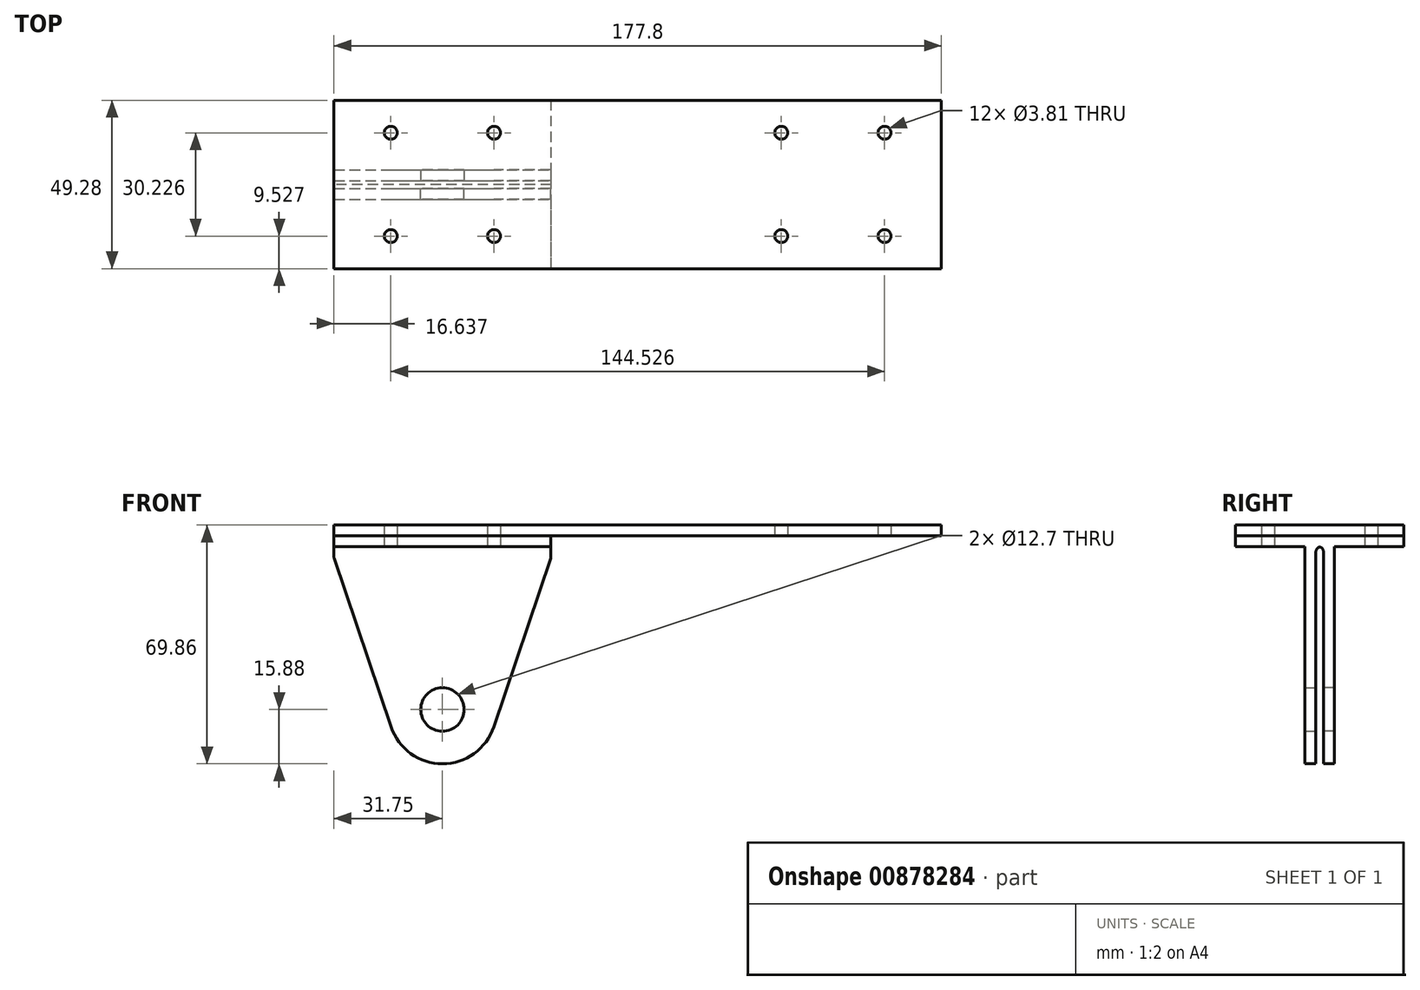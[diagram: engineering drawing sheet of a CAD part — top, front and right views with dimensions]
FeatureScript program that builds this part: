
annotation { "Feature Type Name" : "Feature", "Feature Type Description" : "" }
export const myFeature = defineFeature(function(context is Context, id is Id, definition is map)
    precondition{}
    {
        {
            var Q0;
            Q0=qCreatedBy(makeId("Front.planeOp"),FACE);
            var sketch = newSketch(context, id + "F0", { "sketchPlane" : qUnion([Q0])});
            skCircle(sketch, "E0", {"center": v(0, 0) * mm, "radius": 38.1 * mm});
            skSolve(sketch);
        }
        {
            var Q0;
            Q0=qCreatedBy(makeId("Front.planeOp"),FACE);
            cPlane(context, id + "F1", {"entities" : qUnion([Q0]), "cplaneType" : CPlaneType.OFFSET, "offset" : ((1.62 / 2) + .325) * mm, "width" : 152.4 * mm, "height" : 152.4 * mm});
        }
        {
            var Q0;
            Q0=qCreatedBy(id+"F1.planeOp",FACE);
            var sketch = newSketch(context, id + "F2", { "sketchPlane" : qUnion([Q0])});
            skCircle(sketch, "E1", {"center": v(0, 0) * mm, "radius": 6.35 * mm});
            skArc(sketch, "E2", {"start": v(-15.04, -5.07) * mm, "mid": v(0, -15.87) * mm, "end": v(15.04, -5.07) * mm});
            skLineSegment(sketch, "E3.bottom", {"start": v(-31.75, 47.62) * mm, "end": v(31.75, 47.62) * mm});
            skLineSegment(sketch, "E3.top", {"start": v(-31.75, 44.45) * mm, "end": v(31.75, 44.45) * mm});
            skLineSegment(sketch, "E3.left", {"start": v(-31.75, 47.62) * mm, "end": v(-31.75, 44.45) * mm});
            skLineSegment(sketch, "E3.right", {"start": v(31.75, 47.62) * mm, "end": v(31.75, 44.45) * mm});
            skPoint(sketch, "E3.middle", {"position": v(0, 46.04) * mm});
            skLineSegment(sketch, "E4", {"start": v(-31.75, 44.45) * mm, "end": v(-15.04, -5.07) * mm});
            skLineSegment(sketch, "E5", {"start": v(31.75, 44.45) * mm, "end": v(15.04, -5.07) * mm});
            skSolve(sketch);
        }
        {
            var Q0;
            Q0 = qSketchRegion(id + "F2", true);
            extrude(context, id + "F3", {"entities" : qUnion([Q0]), "depth" : 3.17 * mm, "offsetDistance" : 25.4 * mm});
        }
        {
            var Q0;
            Q0=makeQuery(id+"F3.opExtrude","SWEPT_BODY",BODY,{"disambiguationData":[OSD([sQuery(id+"F2.wireOp",EDGE,"E1"),sQuery(id+"F2.wireOp",EDGE,"E2"),sQuery(id+"F2.wireOp",EDGE,"E3.bottom"),sQuery(id+"F2.wireOp",EDGE,"E3.left"),sQuery(id+"F2.wireOp",EDGE,"E3.right"),sQuery(id+"F2.wireOp",EDGE,"E4"),sQuery(id+"F2.wireOp",EDGE,"E5")])]});
            var Q1;
            Q1=qCreatedBy(makeId("Front.planeOp"),FACE);
            mirror(context, id + "F4", {"entities" : qUnion([Q0]), "mirrorPlane" : qUnion([Q1])});
        }
        {
            var Q0;
            Q0=makeQuery(id+"F4.opPattern","COPY",FACE,{"derivedFrom":makeQuery(id+"F3.opExtrude","SWEPT_FACE",FACE,{"disambiguationData":[OSD([sQuery(id+"F2.wireOp",EDGE,"E3.bottom")])]}),"instanceName":"1"});
            var sketch = newSketch(context, id + "F5", { "sketchPlane" : qUnion([Q0])});
            skLineSegment(sketch, "E6.bottom", {"start": v(-31.75, 24.64) * mm, "end": v(31.75, 24.64) * mm});
            skLineSegment(sketch, "E6.top", {"start": v(-31.75, -24.64) * mm, "end": v(31.75, -24.64) * mm});
            skLineSegment(sketch, "E6.left", {"start": v(-31.75, 24.64) * mm, "end": v(-31.75, -24.64) * mm});
            skLineSegment(sketch, "E6.right", {"start": v(31.75, 24.64) * mm, "end": v(31.75, -24.64) * mm});
            skLineSegment(sketch, "E7.bottom", {"start": v(-15.11, 15.11) * mm, "end": v(15.11, 15.11) * mm, "construction": true});
            skLineSegment(sketch, "E7.top", {"start": v(-15.11, -15.11) * mm, "end": v(15.11, -15.11) * mm, "construction": true});
            skLineSegment(sketch, "E7.left", {"start": v(-15.11, 15.11) * mm, "end": v(-15.11, -15.11) * mm, "construction": true});
            skLineSegment(sketch, "E7.right", {"start": v(15.11, 15.11) * mm, "end": v(15.11, -15.11) * mm, "construction": true});
            skPoint(sketch, "E7.middle", {"position": v(0, 0) * mm});
            skCircle(sketch, "E8", {"center": v(-15.11, -15.11) * mm, "radius": 1.9 * mm});
            skCircle(sketch, "E9.MirrorC", {"center": v(-15.11, 15.11) * mm, "radius": 1.9 * mm});
            skCircle(sketch, "E10.MirrorC", {"center": v(15.11, 15.11) * mm, "radius": 1.9 * mm});
            skCircle(sketch, "E11.MirrorC", {"center": v(15.11, -15.11) * mm, "radius": 1.9 * mm});
            skSolve(sketch);
        }
        {
            var Q0;
            Q0 = qSketchRegion(id + "F5", true);
            extrude(context, id + "F6", {"entities" : qUnion([Q0]), "operationType" : NewBodyOperationType.ADD, "depth" : 3.17 * mm, "offsetDistance" : 25.4 * mm});
        }
        {
            var Q0;
            Q0=makeQuery(id+"F6.opExtrude","CAP_FACE",FACE,{"disambiguationData":[OSD([sQuery(id+"F5.wireOp",EDGE,"E6.bottom"),sQuery(id+"F5.wireOp",EDGE,"E6.top"),sQuery(id+"F5.wireOp",EDGE,"E6.left"),sQuery(id+"F5.wireOp",EDGE,"E6.right"),sQuery(id+"F5.wireOp",EDGE,"E8"),sQuery(id+"F5.wireOp",EDGE,"E9.MirrorC"),sQuery(id+"F5.wireOp",EDGE,"E10.MirrorC"),sQuery(id+"F5.wireOp",EDGE,"E11.MirrorC")])],"isStart":false});
            var sketch = newSketch(context, id + "F7", { "sketchPlane" : qUnion([Q0])});
            skLineSegment(sketch, "E12.bottom", {"start": v(-31.75, 24.64) * mm, "end": v(146.05, 24.64) * mm});
            skLineSegment(sketch, "E12.top", {"start": v(-31.75, -24.64) * mm, "end": v(146.05, -24.64) * mm});
            skLineSegment(sketch, "E12.left", {"start": v(-31.75, 24.64) * mm, "end": v(-31.75, -24.64) * mm});
            skLineSegment(sketch, "E12.right", {"start": v(146.05, 24.64) * mm, "end": v(146.05, -24.64) * mm});
            skCircle(sketch, "E13.0", {"center": v(-15.11, 15.11) * mm, "radius": 1.9 * mm});
            skCircle(sketch, "E14.0", {"center": v(15.11, 15.11) * mm, "radius": 1.9 * mm});
            skCircle(sketch, "E15.0", {"center": v(-15.11, -15.11) * mm, "radius": 1.9 * mm});
            skCircle(sketch, "E16.0", {"center": v(15.11, -15.11) * mm, "radius": 1.9 * mm});
            skLineSegment(sketch, "E17", {"start": v(57.15, 24.64) * mm, "end": v(57.15, -24.64) * mm, "construction": true});
            skCircle(sketch, "E18.MirrorC", {"center": v(129.41, -15.11) * mm, "radius": 1.9 * mm});
            skCircle(sketch, "E19.MirrorC", {"center": v(99.19, -15.11) * mm, "radius": 1.9 * mm});
            skCircle(sketch, "E20.MirrorC", {"center": v(129.41, 15.11) * mm, "radius": 1.9 * mm});
            skCircle(sketch, "E21.MirrorC", {"center": v(99.19, 15.11) * mm, "radius": 1.9 * mm});
            skSolve(sketch);
        }
        {
            var Q0;
            Q0 = qSketchRegion(id + "F7", true);
            extrude(context, id + "F8", {"entities" : qUnion([Q0]), "depth" : 3.17 * mm, "offsetDistance" : 25.4 * mm});
        }
        {
            var Q0;
            Q0=makeQuery(id+"F3.opExtrude","CAP_EDGE",EDGE,{"disambiguationData":[OSD([sQuery(id+"F2.wireOp",EDGE,"E3.bottom")])],"isStart":true});
            var Q1;
            Q1=makeQuery(id+"F3.opExtrude","SWEPT_EDGE",EDGE,{"disambiguationData":[OSD([sQuery(id+"F2.wireOp",EDGE,"E3.top"),sQuery(id+"F2.wireOp",EDGE,"E3.left"),sQuery(id+"F2.wireOp",EDGE,"E4")])]});
            var Q2;
            Q2=makeQuery(id+"F4.opPattern","COPY",EDGE,{"derivedFrom":makeQuery(id+"F3.opExtrude","SWEPT_EDGE",EDGE,{"disambiguationData":[OSD([sQuery(id+"F2.wireOp",EDGE,"E3.top"),sQuery(id+"F2.wireOp",EDGE,"E3.left"),sQuery(id+"F2.wireOp",EDGE,"E4")])]}),"instanceName":"1"});
            var Q3;
            Q3=makeQuery(id+"F4.opPattern","COPY",EDGE,{"derivedFrom":makeQuery(id+"F3.opExtrude","CAP_EDGE",EDGE,{"disambiguationData":[OSD([sQuery(id+"F2.wireOp",EDGE,"E3.bottom")])],"isStart":true}),"instanceName":"1"});
            var Q4;
            Q4=makeQuery(id+"F4.opPattern","COPY",EDGE,{"derivedFrom":makeQuery(id+"F3.opExtrude","SWEPT_EDGE",EDGE,{"disambiguationData":[OSD([sQuery(id+"F2.wireOp",EDGE,"E3.top"),sQuery(id+"F2.wireOp",EDGE,"E3.right"),sQuery(id+"F2.wireOp",EDGE,"E5")])]}),"instanceName":"1"});
            var Q5;
            Q5=makeQuery(id+"F3.opExtrude","SWEPT_EDGE",EDGE,{"disambiguationData":[OSD([sQuery(id+"F2.wireOp",EDGE,"E3.top"),sQuery(id+"F2.wireOp",EDGE,"E3.right"),sQuery(id+"F2.wireOp",EDGE,"E5")])]});
            fillet(context, id + "F9", {"entities" : qUnion([Q0, Q1, Q2, Q3, Q4, Q5]), "radius" : 1.59 * mm, "tangentPropagation" : true, "allowEdgeOverflow" : false});
        }
    });
